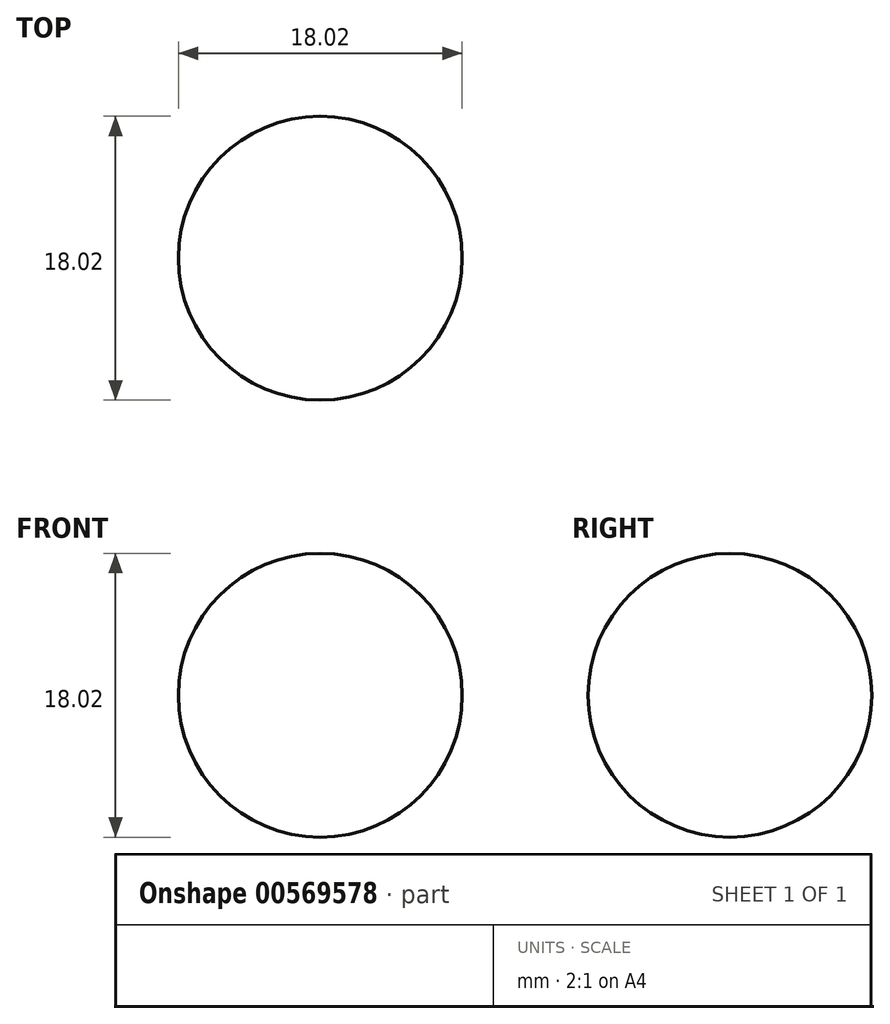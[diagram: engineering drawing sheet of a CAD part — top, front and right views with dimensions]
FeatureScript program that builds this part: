
annotation { "Feature Type Name" : "Feature", "Feature Type Description" : "" }
export const myFeature = defineFeature(function(context is Context, id is Id, definition is map)
    precondition{}
    {
        {
            var Q0;
            Q0=qCreatedBy(makeId("Front.planeOp"),FACE);
            var sketch = newSketch(context, id + "F0", { "sketchPlane" : qUnion([Q0])});
            skCircle(sketch, "E0", {"center": v(0, 0) * mm, "radius": 6.35 * mm});
            skSolve(sketch);
        }
        {
            var Q0;
            Q0=sQuery(id+"F0.wireOp",EDGE,"E0");
            extrude(context, id + "F1", {"bodyType" : ToolBodyType.SURFACE, "surfaceEntities" : qUnion([Q0]), "depth" : 203.2 * mm, "offsetDistance" : 25.4 * mm});
        }
        {
            var Q0;
            Q0=qCreatedBy(makeId("Front.planeOp"),FACE);
            var sketch = newSketch(context, id + "F2", { "sketchPlane" : qUnion([Q0])});
            skArc(sketch, "E1", {"start": v(0, -9.01) * mm, "mid": v(-9.01, 0) * mm, "end": v(0, 9.01) * mm});
            skLineSegment(sketch, "E2", {"start": v(0, 9.01) * mm, "end": v(0, -9.01) * mm});
            skSolve(sketch);
        }
        {
            var Q0;
            Q0 = qSketchRegion(id + "F2", true);
            var Q1;
            Q1=sQuery(id+"F2.wireOp",EDGE,"E2");
            revolve(context, id + "F3", {"entities" : qUnion([Q0]), "axis" : qUnion([Q1]), "revolveType" : RevolveType.FULL});
        }
    });
